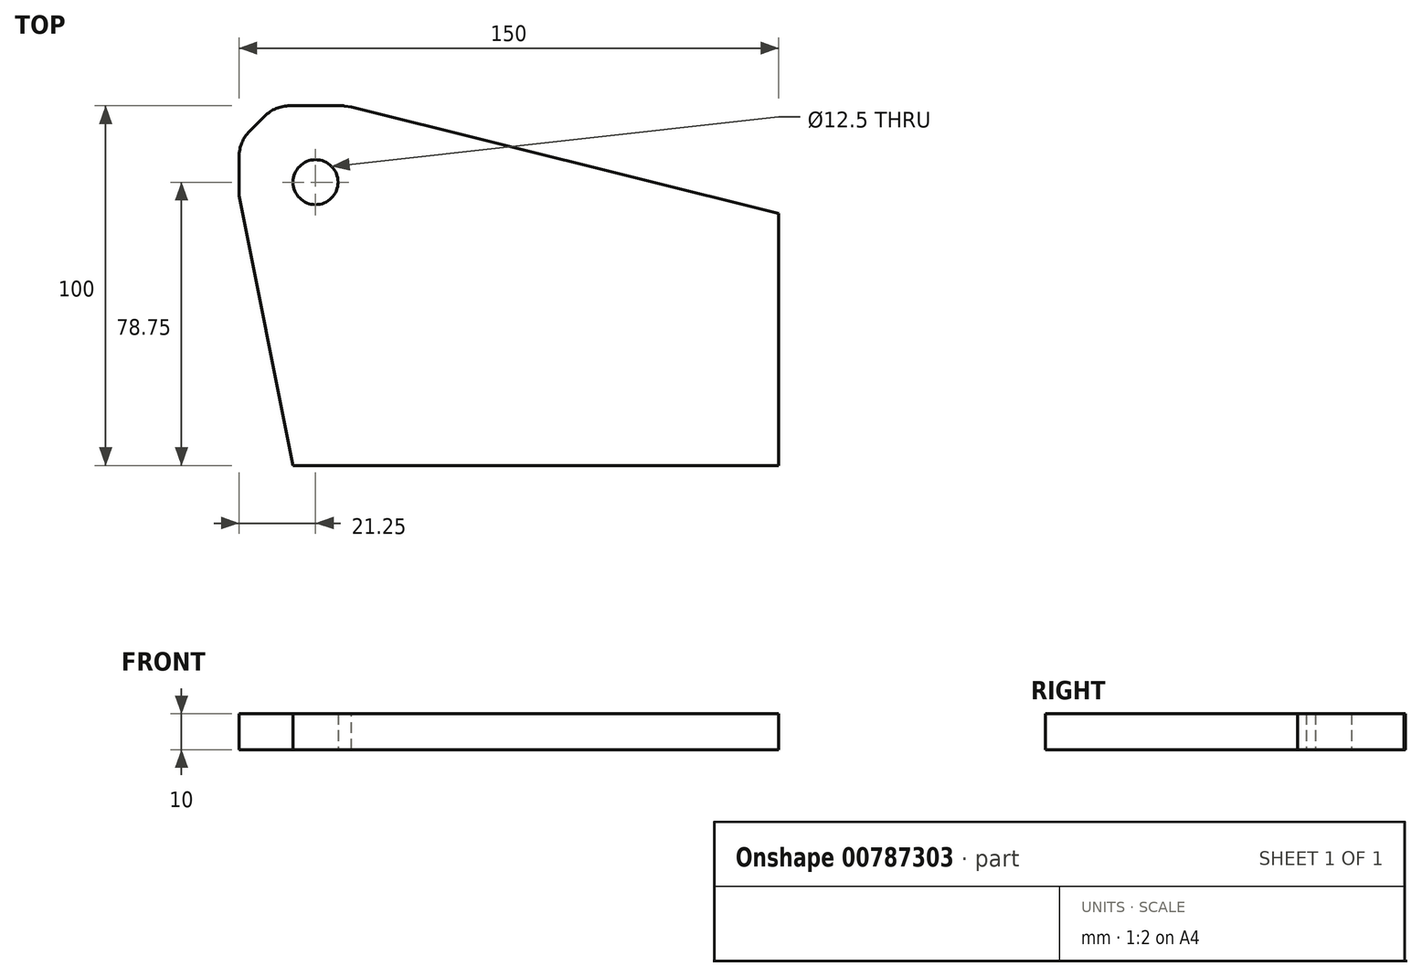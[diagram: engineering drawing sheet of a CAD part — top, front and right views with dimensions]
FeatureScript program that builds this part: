
annotation { "Feature Type Name" : "Feature", "Feature Type Description" : "" }
export const myFeature = defineFeature(function(context is Context, id is Id, definition is map)
    precondition{}
    {
        {
            var Q0;
            Q0=qCreatedBy(makeId("Top.planeOp"),FACE);
            var sketch = newSketch(context, id + "F0", { "sketchPlane" : qUnion([Q0])});
            skLineSegment(sketch, "E0.bottom", {"start": v(15, -1.25) * mm, "end": v(150, -1.25) * mm});
            skLineSegment(sketch, "E0.top", {"start": v(0, 98.75) * mm, "end": v(30, 98.75) * mm});
            skLineSegment(sketch, "E0.right", {"start": v(150, -1.25) * mm, "end": v(150, 68.75) * mm});
            skCircle(sketch, "E1", {"center": v(21.25, 77.5) * mm, "radius": 6.25 * mm});
            skLineSegment(sketch, "E2", {"start": v(0, 73.75) * mm, "end": v(0, 98.75) * mm});
            skCircle(sketch, "E3", {"center": v(21.25, 77.5) * mm, "radius": 21.25 * mm, "construction": true});
            skLineSegment(sketch, "E4", {"start": v(150, 68.75) * mm, "end": v(30, 98.75) * mm});
            skLineSegment(sketch, "E5", {"start": v(0, 73.75) * mm, "end": v(15, -1.25) * mm});
            skSolve(sketch);
        }
        {
            var Q0;
            Q0=makeQuery(id+"F0.imprint","IMPRINT",FACE,{"disambiguationData":[TD([[makeQuery(id+"F0.imprint","IMPRINT",EDGE,{"derivedFrom":sQuery(id+"F0.wireOp",EDGE,"E0.bottom")}),1.0]])]});
            extrude(context, id + "F1", {"entities" : qUnion([Q0]), "depth" : 10 * mm, "offsetDistance" : 25 * mm});
        }
        {
            var Q0;
            Q0=makeQuery(id+"F1.opExtrude","SWEPT_EDGE",EDGE,{"disambiguationData":[OSD([sQuery(id+"F0.wireOp",EDGE,"E0.top"),sQuery(id+"F0.wireOp",EDGE,"E0.left")])]});
            chamfer(context, id + "F2", {"entities" : qUnion([Q0]), "width" : 10 * mm, "tangentPropagation" : true});
        }
        {
            var Q0;
            {var subQ0=sQuery(id+"F0.wireOp",EDGE,"E0.top");Q0=makeQuery(id+"F2.opChamfer","BLEND_EDGE",EDGE,{"blendedFrom":[makeQuery(id+"F1.opExtrude","SWEPT_EDGE",EDGE,{"disambiguationData":[OSD([subQ0,sQuery(id+"F0.wireOp",EDGE,"E0.left")])]}),makeQuery(id+"F1.opExtrude","SWEPT_FACE",FACE,{"disambiguationData":[OSD([subQ0])]})],"blendedInto":[makeQuery(id+"F1.opExtrude","SWEPT_FACE",FACE,{"disambiguationData":[OSD([subQ0])]})]});}
            var Q1;
            Q1=makeQuery(id+"F1.opExtrude","SWEPT_EDGE",EDGE,{"disambiguationData":[OSD([sQuery(id+"F0.wireOp",EDGE,"E0.top"),sQuery(id+"F0.wireOp",EDGE,"V2a9aMAc-e67v-Mynm-u0HB-jDwKRaxKdQhE")])]});
            fillet(context, id + "F3", {"entities" : qUnion([Q0, Q1]), "radius" : 10 * mm, "tangentPropagation" : true, "allowEdgeOverflow" : false});
        }
        {
            var Q0;
            {var subQ0=sQuery(id+"F0.wireOp",EDGE,"E2");Q0=makeQuery(id+"F2.opChamfer","BLEND_EDGE",EDGE,{"blendedFrom":[makeQuery(id+"F1.opExtrude","SWEPT_EDGE",EDGE,{"disambiguationData":[OSD([sQuery(id+"F0.wireOp",EDGE,"E0.top"),subQ0])]}),makeQuery(id+"F1.opExtrude","SWEPT_FACE",FACE,{"disambiguationData":[OSD([subQ0])]})],"blendedInto":[makeQuery(id+"F1.opExtrude","SWEPT_FACE",FACE,{"disambiguationData":[OSD([subQ0])]})]});}
            fillet(context, id + "F4", {"entities" : qUnion([Q0]), "radius" : 10 * mm, "tangentPropagation" : true, "allowEdgeOverflow" : false});
        }
    });
